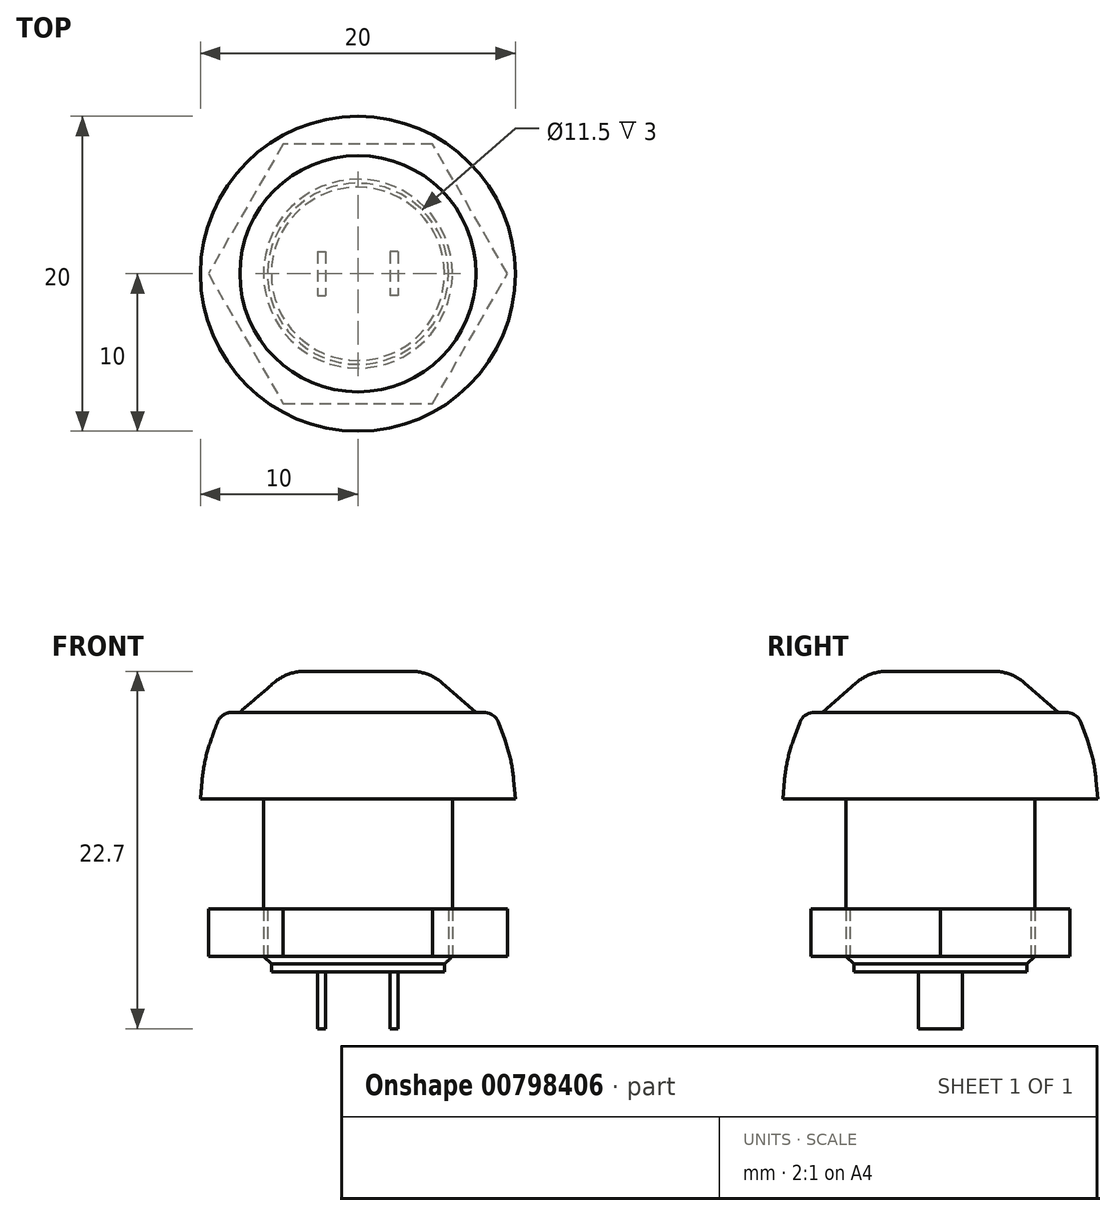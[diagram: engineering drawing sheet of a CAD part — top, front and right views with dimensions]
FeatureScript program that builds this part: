
annotation { "Feature Type Name" : "Feature", "Feature Type Description" : "" }
export const myFeature = defineFeature(function(context is Context, id is Id, definition is map)
    precondition{}
    {
        {
            var Q0;
            Q0=qCreatedBy(makeId("Top.planeOp"),FACE);
            var sketch = newSketch(context, id + "F0", { "sketchPlane" : qUnion([Q0])});
            skCircle(sketch, "E0", {"center": v(0, 0) * mm, "radius": 6 * mm});
            skSolve(sketch);
        }
        {
            var Q0;
            Q0 = qSketchRegion(id + "F0", true);
            extrude(context, id + "F1", {"entities" : qUnion([Q0]), "depth" : 10 * mm, "offsetDistance" : 25 * mm});
        }
        {
            var Q0;
            Q0=qCreatedBy(makeId("Front.planeOp"),FACE);
            var sketch = newSketch(context, id + "F2", { "sketchPlane" : qUnion([Q0])});
            skLineSegment(sketch, "E1", {"start": v(0, 0) * mm, "end": v(0, -2.63) * mm, "construction": true});
            skLineSegment(sketch, "E2", {"start": v(6, 0) * mm, "end": v(5.5, -0.5) * mm});
            skLineSegment(sketch, "E3", {"start": v(5.5, -0.5) * mm, "end": v(5.5, -1) * mm});
            skLineSegment(sketch, "E4", {"start": v(5.5, -1) * mm, "end": v(0, -1) * mm});
            skLineSegment(sketch, "E5", {"start": v(0, -1) * mm, "end": v(0, 0) * mm});
            skLineSegment(sketch, "E6", {"start": v(0, 0) * mm, "end": v(6, 0) * mm});
            skSolve(sketch);
        }
        {
            var Q0;
            Q0 = qSketchRegion(id + "F2", true);
            var Q1;
            Q1=sQuery(id+"F2.wireOp",EDGE,"E1");
            revolve(context, id + "F3", {"operationType" : NewBodyOperationType.ADD, "surfaceOperationType" : NewSurfaceOperationType.NEW, "entities" : qUnion([Q0]), "axis" : qUnion([Q1]), "revolveType" : RevolveType.FULL});
        }
        {
            var Q0;
            Q0=makeQuery(id+"F3.opRevolve","SWEPT_FACE",FACE,{"disambiguationData":[OSD([sQuery(id+"F2.wireOp",EDGE,"E4")])]});
            var sketch = newSketch(context, id + "F4", { "sketchPlane" : qUnion([Q0])});
            skLineSegment(sketch, "E7", {"start": v(0, -4.27) * mm, "end": v(0, 4.85) * mm, "construction": true});
            skLineSegment(sketch, "E8", {"start": v(5.42, 0) * mm, "end": v(-5.56, 0) * mm, "construction": true});
            skLineSegment(sketch, "E9.bottom", {"start": v(2.55, -1.4) * mm, "end": v(2.05, -1.4) * mm});
            skLineSegment(sketch, "E9.top", {"start": v(2.55, 1.4) * mm, "end": v(2.05, 1.4) * mm});
            skLineSegment(sketch, "E9.left", {"start": v(2.55, -1.4) * mm, "end": v(2.55, 1.4) * mm});
            skLineSegment(sketch, "E9.right", {"start": v(2.05, -1.4) * mm, "end": v(2.05, 1.4) * mm});
            skPoint(sketch, "E9.middle", {"position": v(2.3, 0) * mm});
            skLineSegment(sketch, "E10.MirrorCS", {"start": v(-2.55, -1.4) * mm, "end": v(-2.55, 1.4) * mm});
            skPoint(sketch, "E11.MirrorP", {"position": v(-2.3, 0) * mm});
            skLineSegment(sketch, "E12.MirrorCS", {"start": v(-2.55, -1.4) * mm, "end": v(-2.05, -1.4) * mm});
            skLineSegment(sketch, "E13.MirrorCS", {"start": v(-2.55, 1.4) * mm, "end": v(-2.05, 1.4) * mm});
            skLineSegment(sketch, "E14.MirrorCS", {"start": v(-2.05, -1.4) * mm, "end": v(-2.05, 1.4) * mm});
            skSolve(sketch);
        }
        {
            var Q0;
            Q0 = qSketchRegion(id + "F4", true);
            extrude(context, id + "F5", {"entities" : qUnion([Q0]), "depth" : 3.6 * mm, "offsetDistance" : 25 * mm});
        }
        {
            var Q0;
            Q0=qCreatedBy(makeId("Front.planeOp"),FACE);
            var sketch = newSketch(context, id + "F6", { "sketchPlane" : qUnion([Q0])});
            skLineSegment(sketch, "E15", {"start": v(0, 0) * mm, "end": v(0, 28.38) * mm, "construction": true});
            skLineSegment(sketch, "E16", {"start": v(0, 10) * mm, "end": v(10, 10) * mm});
            skLineSegment(sketch, "E17", {"start": v(10, 10) * mm, "end": v(9.9, 11.19) * mm});
            skLineSegment(sketch, "E18", {"start": v(9.33, 13.74) * mm, "end": v(8.93, 14.84) * mm});
            skLineSegment(sketch, "E19", {"start": v(7.99, 15.5) * mm, "end": v(0, 15.5) * mm});
            skPoint(sketch, "E20.visualSharp", {"position": v(9.78, 12.5) * mm});
            skArc(sketch, "E20.filletArc", {"start": v(9.9, 11.19) * mm, "mid": v(9.7, 12.48) * mm, "end": v(9.33, 13.74) * mm});
            skPoint(sketch, "E21.visualSharp", {"position": v(8.69, 15.5) * mm});
            skArc(sketch, "E21.filletArc", {"start": v(8.93, 14.84) * mm, "mid": v(8.56, 15.32) * mm, "end": v(7.99, 15.5) * mm});
            skLineSegment(sketch, "E22", {"start": v(0, 10) * mm, "end": v(0, 15.5) * mm});
            skSolve(sketch);
        }
        {
            var Q0;
            Q0 = qSketchRegion(id + "F6", true);
            var Q1;
            Q1=sQuery(id+"F6.wireOp",EDGE,"E15");
            revolve(context, id + "F7", {"operationType" : NewBodyOperationType.ADD, "surfaceOperationType" : NewSurfaceOperationType.NEW, "entities" : qUnion([Q0]), "axis" : qUnion([Q1]), "revolveType" : RevolveType.FULL});
        }
        {
            var Q0;
            Q0=qCreatedBy(makeId("Front.planeOp"),FACE);
            var sketch = newSketch(context, id + "F8", { "sketchPlane" : qUnion([Q0])});
            skLineSegment(sketch, "E23", {"start": v(0, 0) * mm, "end": v(0, 19.61) * mm, "construction": true});
            skLineSegment(sketch, "E24", {"start": v(0, 15.5) * mm, "end": v(7.5, 15.5) * mm});
            skLineSegment(sketch, "E25", {"start": v(7.5, 15.5) * mm, "end": v(5.35, 17.37) * mm});
            skLineSegment(sketch, "E26", {"start": v(3.38, 18.1) * mm, "end": v(0, 18.1) * mm});
            skLineSegment(sketch, "E27", {"start": v(0, 18.1) * mm, "end": v(0, 15.5) * mm});
            skPoint(sketch, "E28.visualSharp", {"position": v(4.5, 18.1) * mm});
            skArc(sketch, "E28.filletArc", {"start": v(5.35, 17.37) * mm, "mid": v(4.43, 17.91) * mm, "end": v(3.38, 18.1) * mm});
            skSolve(sketch);
        }
        {
            var Q0;
            Q0 = qSketchRegion(id + "F8", true);
            var Q1;
            Q1=sQuery(id+"F8.wireOp",EDGE,"E23");
            revolve(context, id + "F9", {"surfaceOperationType" : NewSurfaceOperationType.NEW, "entities" : qUnion([Q0]), "axis" : qUnion([Q1]), "revolveType" : RevolveType.FULL});
        }
        {
            var Q0;
            Q0=qCreatedBy(makeId("Top.planeOp"),FACE);
            var sketch = newSketch(context, id + "F10", { "sketchPlane" : qUnion([Q0])});
            skCircle(sketch, "E29", {"center": v(0, 0) * mm, "radius": 9.5 * mm, "construction": true});
            skLineSegment(sketch, "E30", {"start": v(-4.75, -8.23) * mm, "end": v(4.75, -8.23) * mm});
            skLineSegment(sketch, "E31", {"start": v(4.75, -8.23) * mm, "end": v(9.5, 0) * mm});
            skLineSegment(sketch, "E32", {"start": v(9.5, 0) * mm, "end": v(4.75, 8.23) * mm});
            skLineSegment(sketch, "E33", {"start": v(4.75, 8.23) * mm, "end": v(-4.75, 8.23) * mm});
            skLineSegment(sketch, "E34", {"start": v(-4.75, 8.23) * mm, "end": v(-9.5, 0) * mm});
            skLineSegment(sketch, "E35", {"start": v(-9.5, 0) * mm, "end": v(-4.75, -8.23) * mm});
            skCircle(sketch, "E36", {"center": v(0, 0) * mm, "radius": 5.75 * mm});
            skSolve(sketch);
        }
        {
            var Q0;
            Q0 = qSketchRegion(id + "F10", true);
            extrude(context, id + "F11", {"entities" : qUnion([Q0]), "depth" : 3 * mm, "offsetDistance" : 25 * mm});
        }
    });
